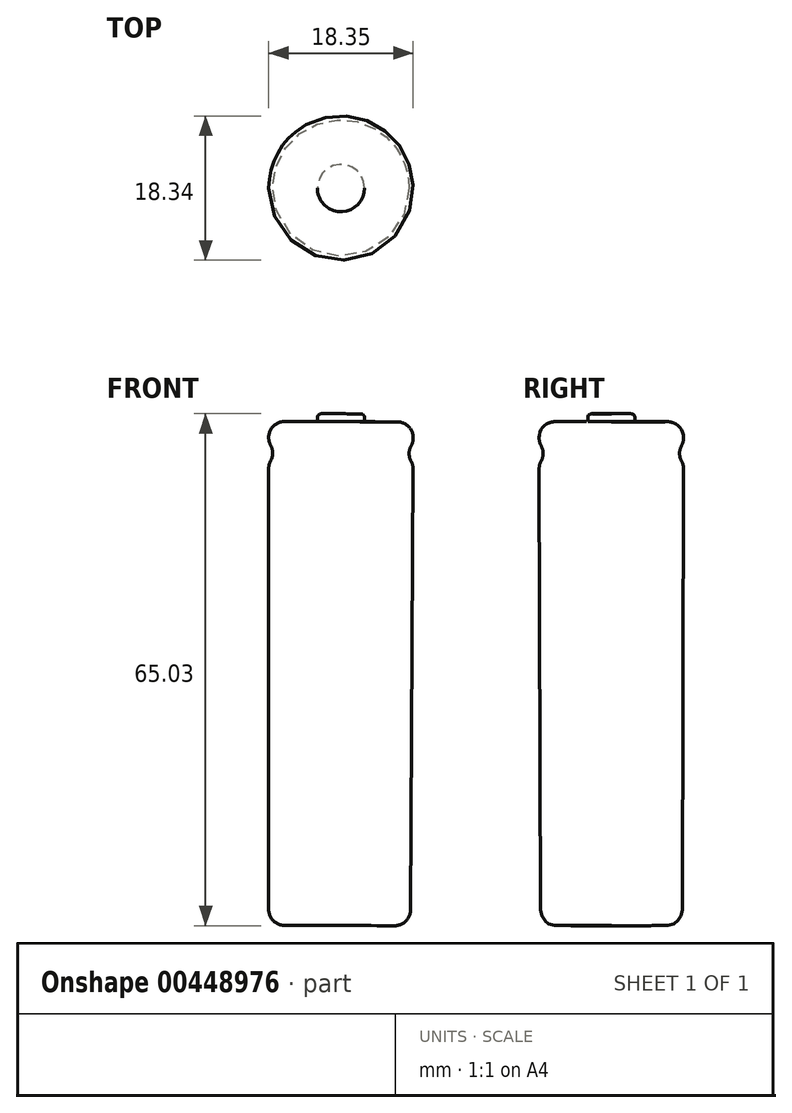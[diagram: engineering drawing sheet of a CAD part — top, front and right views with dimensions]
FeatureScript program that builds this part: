
annotation { "Feature Type Name" : "Feature", "Feature Type Description" : "" }
export const myFeature = defineFeature(function(context is Context, id is Id, definition is map)
    precondition{}
    {
        {
            var Q0;
            Q0=qCreatedBy(makeId("Front.planeOp"),FACE);
            var sketch = newSketch(context, id + "F2", { "sketchPlane" : qUnion([Q0])});
            skLineSegment(sketch, "E0", {"start": v(0, -24.86) * mm, "end": v(-9, -24.86) * mm});
            skLineSegment(sketch, "E1", {"start": v(-9, -24.86) * mm, "end": v(-9, 33.66) * mm});
            skLineSegment(sketch, "E2", {"start": v(-9, 33.66) * mm, "end": v(-9, 33.81) * mm});
            skLineSegment(sketch, "E3", {"start": v(-9, 39.13) * mm, "end": v(-2.82, 39.13) * mm});
            skLineSegment(sketch, "E4", {"start": v(-2.82, 39.13) * mm, "end": v(-2.82, 39.63) * mm});
            skLineSegment(sketch, "E5", {"start": v(-2.32, 40.13) * mm, "end": v(0.18, 40.13) * mm});
            skLineSegment(sketch, "E6", {"start": v(0.18, 40.13) * mm, "end": v(0, -24.86) * mm});
            skPoint(sketch, "E7.visualSharp", {"position": v(-2.82, 40.13) * mm});
            skArc(sketch, "E7.filletArc", {"start": v(-2.32, 40.13) * mm, "mid": v(-2.67, 39.99) * mm, "end": v(-2.82, 39.63) * mm});
            skArc(sketch, "E8", {"start": v(-9, 33.81) * mm, "mid": v(-8.5, 35.13) * mm, "end": v(-9, 36.46) * mm});
            skLineSegment(sketch, "E9.trimOffspring", {"start": v(-9, 36.46) * mm, "end": v(-9, 39.13) * mm});
            skSolve(sketch);
        }
        {
            var Q0;
            Q0=makeQuery(id+"F2.imprint","IMPRINT",FACE,{"disambiguationData":[TD([[makeQuery(id+"F2.imprint","IMPRINT",EDGE,{"derivedFrom":sQuery(id+"F2.wireOp",EDGE,"E0")}),-1.0]])]});
            var Q1;
            Q1=sQuery(id+"F2.wireOp",EDGE,"E6");
            revolve(context, id + "F3", {"entities" : qUnion([Q0]), "axis" : qUnion([Q1]), "revolveType" : RevolveType.FULL});
        }
        {
            var Q0;
            Q0=makeQuery(id+"F3.opRevolve","SWEPT_EDGE",EDGE,{"disambiguationData":[OSD([sQuery(id+"F2.wireOp",EDGE,"E3"),sQuery(id+"F2.wireOp",EDGE,"E9.trimOffspring")])]});
            var Q1;
            Q1=makeQuery(id+"F3.opRevolve","SWEPT_EDGE",EDGE,{"disambiguationData":[OSD([sQuery(id+"F2.wireOp",EDGE,"E2"),sQuery(id+"F2.wireOp",EDGE,"E8")])]});
            var Q2;
            Q2=makeQuery(id+"F3.opRevolve","SWEPT_EDGE",EDGE,{"disambiguationData":[OSD([sQuery(id+"F2.wireOp",EDGE,"E8"),sQuery(id+"F2.wireOp",EDGE,"E9.trimOffspring")])]});
            var Q3;
            Q3=makeQuery(id+"F3.opRevolve","SWEPT_EDGE",EDGE,{"disambiguationData":[OSD([sQuery(id+"F2.wireOp",EDGE,"E0"),sQuery(id+"F2.wireOp",EDGE,"E1")])]});
            fillet(context, id + "F0", {"entities" : qUnion([Q0, Q1, Q2, Q3]), "radius" : 2 * mm, "tangentPropagation" : true, "allowEdgeOverflow" : false});
        }
    });
